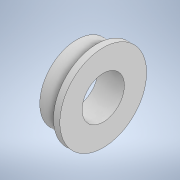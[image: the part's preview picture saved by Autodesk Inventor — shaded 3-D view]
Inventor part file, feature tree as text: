
AUTODESK INVENTOR PART (.ipt)
format: ipt  version: 2020 (Build 240168000, 168)  size: 114,688 bytes
history: native  units: in
note: dims shown in document units (in); Inventor stores cm internally (conversion verified against a paired STEP export)
features: extrude x2, sketch x2
ambient origin geometry x8: Origin, YZ Plane, XZ Plane, XY Plane, X Axis, Y Axis, Z Axis, Center Point
bodies: Solid1 (feature_tree)
feature tree (4):
  extrude  "Extrusion1"  Depth=0.2756in
  extrude  "Extrusion2"  Depth=0.0236in
  sketch  "Sketch1"  dims[d0=0.1575in d1=0.2756in]
  sketch  "Sketch2"  dims[d2=0.0984in d3=0.0in d4=0.3228in d5=0.1575in d6=0.0236in d7=0.0in]
